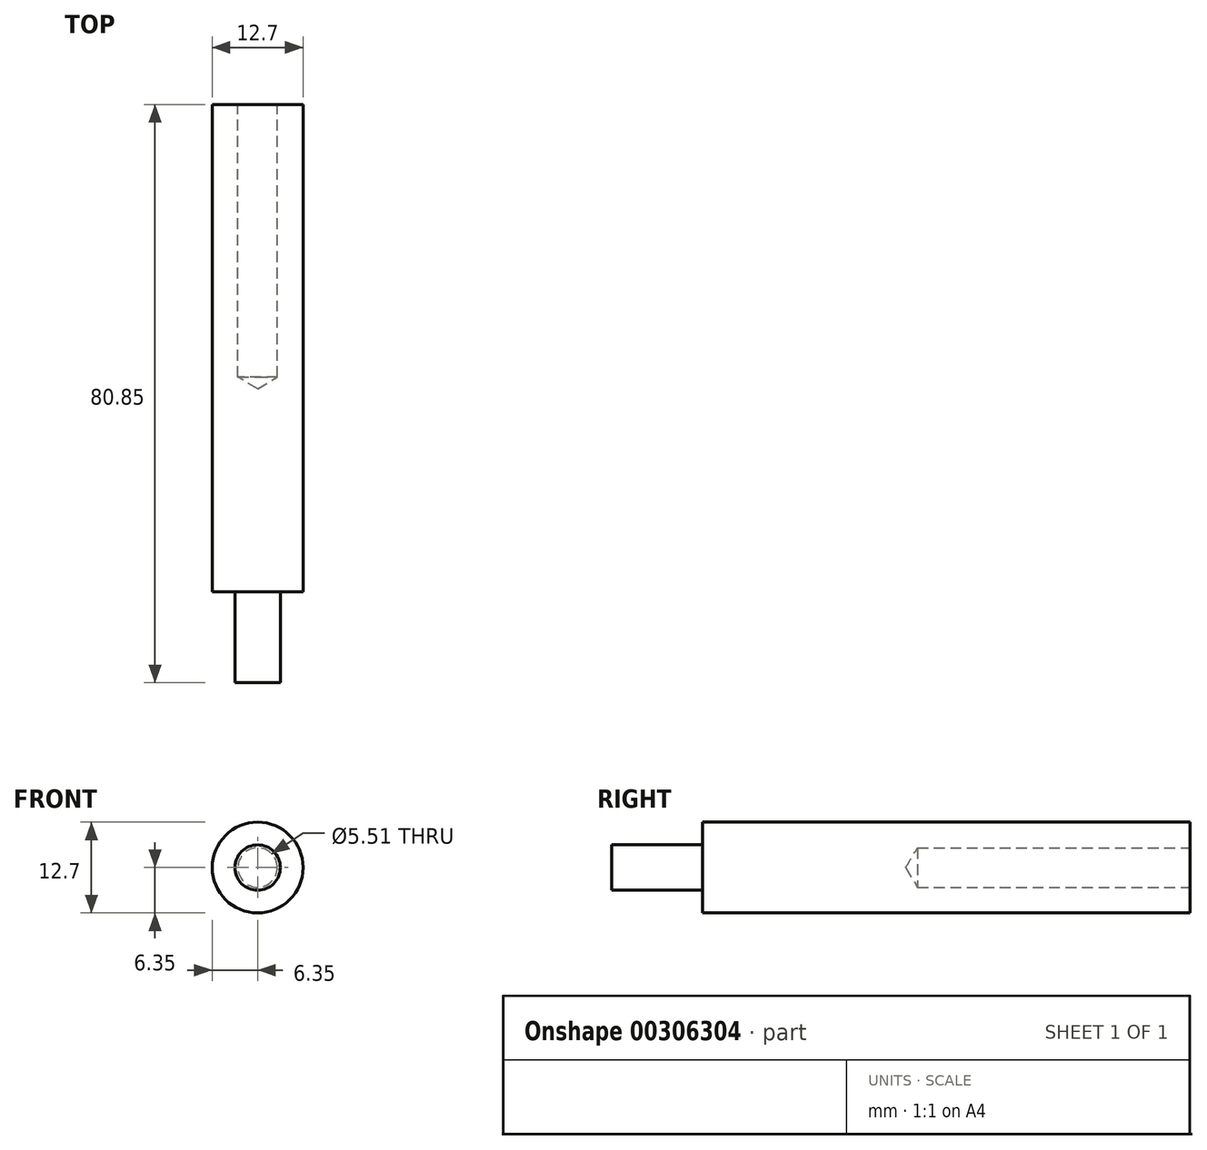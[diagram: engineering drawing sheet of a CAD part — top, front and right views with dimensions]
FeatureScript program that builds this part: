
annotation { "Feature Type Name" : "Feature", "Feature Type Description" : "" }
export const myFeature = defineFeature(function(context is Context, id is Id, definition is map)
    precondition{}
    {
        {
            var Q0;
            Q0=qCreatedBy(makeId("Front.planeOp"),FACE);
            var sketch = newSketch(context, id + "F0", { "sketchPlane" : qUnion([Q0])});
            skCircle(sketch, "E0", {"center": v(0, 0) * mm, "radius": 6.35 * mm});
            skSolve(sketch);
        }
        {
            var Q0;
            Q0=makeQuery(id+"F0.imprint","IMPRINT",FACE,{"disambiguationData":[TD([[makeQuery(id+"F0.imprint","IMPRINT",EDGE,{"derivedFrom":sQuery(id+"F0.wireOp",EDGE,"E0")}),1.0]])]});
            extrude(context, id + "F1", {"entities" : qUnion([Q0]), "depth" : 93.55 * mm});
        }
        {
            var Q0;
            Q0=makeQuery(id+"F1.opExtrude","CAP_FACE",FACE,{"disambiguationData":[OSD([sQuery(id+"F0.wireOp",EDGE,"E0")])],"isStart":false});
            var sketch = newSketch(context, id + "F2", { "sketchPlane" : qUnion([Q0])});
            skCircle(sketch, "E1", {"center": v(0, 0) * mm, "radius": 7.62 * mm});
            skCircle(sketch, "E2", {"center": v(0, 0) * mm, "radius": 3.18 * mm});
            skSolve(sketch);
        }
        {
            var Q0;
            Q0=makeQuery(id+"F2.imprint","IMPRINT",FACE,{"disambiguationData":[TD([[makeQuery(id+"F2.imprint","IMPRINT",EDGE,{"derivedFrom":sQuery(id+"F2.wireOp",EDGE,"E2")}),-1.0]])]});
            extrude(context, id + "F3", {"entities" : qUnion([Q0]), "operationType" : NewBodyOperationType.REMOVE, "oppositeDirection" : true, "depth" : 12.7 * mm});
        }
        {
            var Q0;
            Q0=makeQuery(id+"F1.opExtrude","CAP_FACE",FACE,{"disambiguationData":[OSD([sQuery(id+"F0.wireOp",EDGE,"E0")])],"isStart":true});
            var sketch = newSketch(context, id + "F4", { "sketchPlane" : qUnion([Q0])});
            skPoint(sketch, "E3", {"position": v(0, 0) * mm});
            skSolve(sketch);
        }
        {
            var Q0;
            Q0=sQuery(id+"F4.wireOp",VERTEX,"E3");
            var Q1;
            Q1=makeQuery(id+"F1.opExtrude","SWEPT_BODY",BODY,{"disambiguationData":[OSD([sQuery(id+"F0.wireOp",EDGE,"E0")])]});
            hole(context, id + "F5", {"style" : HoleStyle.C_BORE, "endStyle" : HoleEndStyle.BLIND, "holeDiameter" : 5.5 * mm, "cBoreDiameter" : 12.7 * mm, "cBoreDepth" : 12.7 * mm, "holeDepth" : 50.8 * mm, "tappedDepth" : 12.7 * mm, "tapClearance" : 3, "locations" : qUnion([Q0]), "scope" : qUnion([Q1])});
        }
    });
